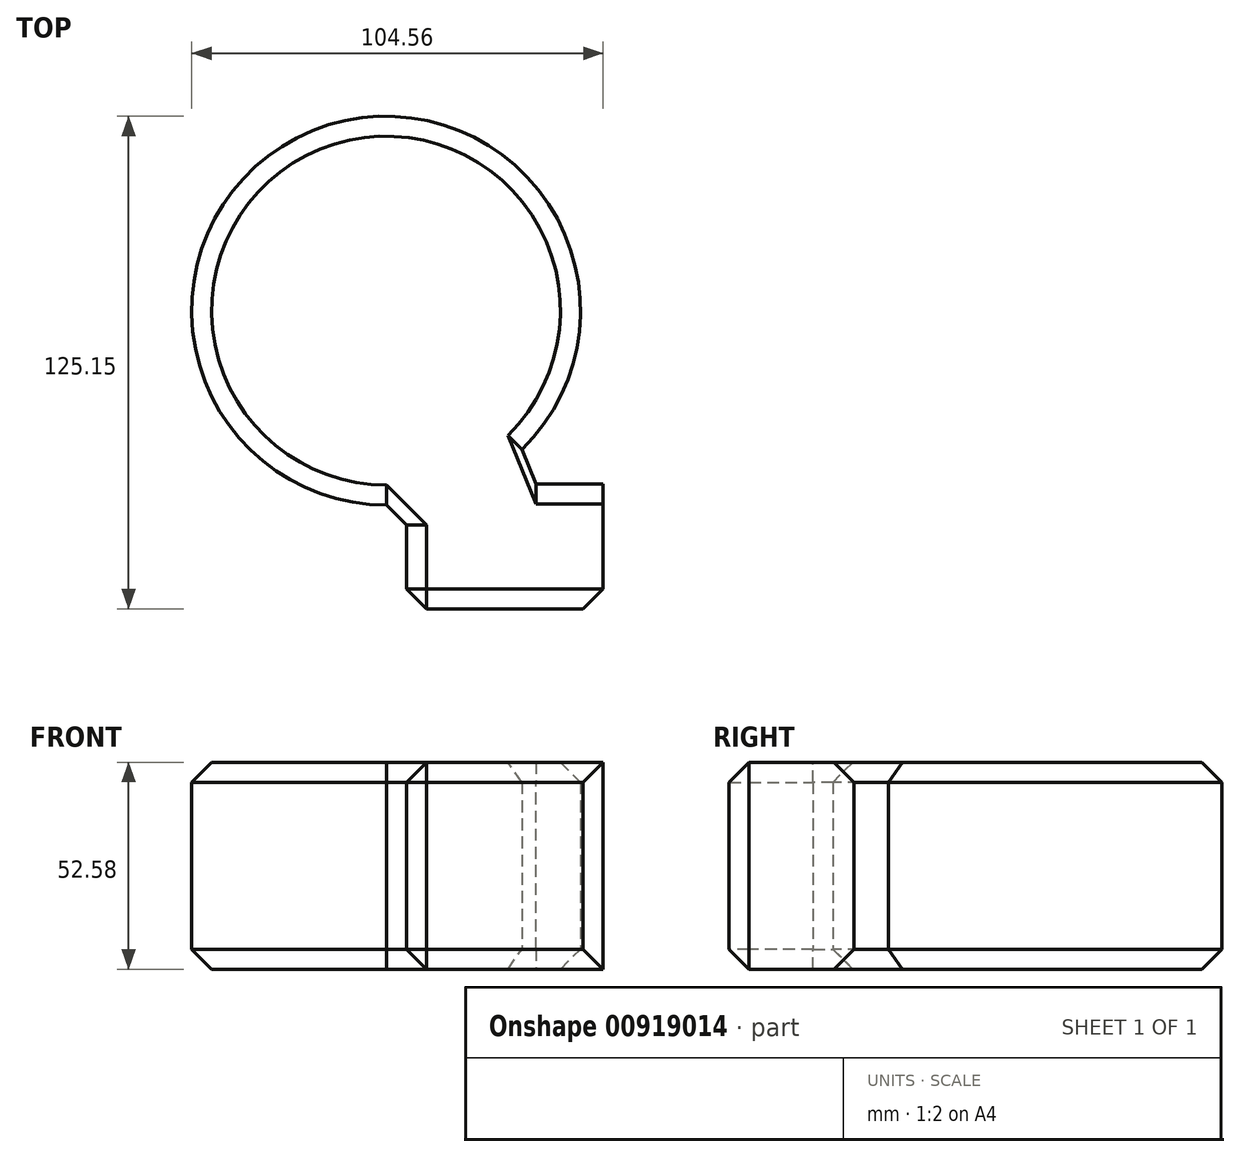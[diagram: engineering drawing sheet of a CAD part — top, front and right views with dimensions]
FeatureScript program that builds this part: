
annotation { "Feature Type Name" : "Feature", "Feature Type Description" : "" }
export const myFeature = defineFeature(function(context is Context, id is Id, definition is map)
    precondition{}
    {
        {
            var Q0;
            Q0=qCreatedBy(makeId("Top.planeOp"),FACE);
            var sketch = newSketch(context, id + "F0", { "sketchPlane" : qUnion([Q0])});
            skLineSegment(sketch, "E0.bottom", {"start": v(-136.07, -9.28) * mm, "end": v(-86.15, -9.28) * mm});
            skLineSegment(sketch, "E0.top", {"start": v(-136.07, -41) * mm, "end": v(-86.15, -41) * mm});
            skLineSegment(sketch, "E0.left", {"start": v(-136.07, -9.28) * mm, "end": v(-136.07, -41) * mm});
            skLineSegment(sketch, "E0.right", {"start": v(-86.15, -9.28) * mm, "end": v(-86.15, -41) * mm});
            skCircle(sketch, "E1", {"center": v(-141.33, 34.78) * mm, "radius": 49.38 * mm});
            skSolve(sketch);
        }
        {
            var Q0;
            Q0 = qSketchRegion(id + "F0", true);
            extrude(context, id + "F1", {"entities" : qUnion([Q0]), "depth" : 52.58 * mm, "offsetDistance" : 25.4 * mm});
        }
        {
            var Q0;
            Q0=makeQuery(id+"F1.opExtrude","SWEPT_FACE",FACE,{"disambiguationData":[OSD([sQuery(id+"F0.wireOp",EDGE,"E0.top")])]});
            var Q1;
            Q1=makeQuery(id+"F1.opExtrude","SWEPT_FACE",FACE,{"disambiguationData":[OSD([sQuery(id+"F0.wireOp",EDGE,"E1")])]});
            chamfer(context, id + "F2", {"entities" : qUnion([Q0, Q1]), "width" : 5.08 * mm, "tangentPropagation" : true});
        }
    });
